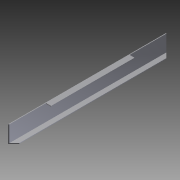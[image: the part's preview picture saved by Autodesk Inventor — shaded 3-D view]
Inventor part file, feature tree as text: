
AUTODESK INVENTOR PART (.ipt)
format: ipt  version: 2012 (Build 160160000, 160)  size: 99,328 bytes
history: native  units: in
note: dims shown in document units (in); Inventor stores cm internally (conversion verified against a paired STEP export)
features: extrude x3, sketch x2
ambient origin geometry x8: Origin, YZ Plane, XZ Plane, XY Plane, X Axis, Y Axis, Z Axis, Center Point
bodies: Solid1 (feature_tree)
feature tree (5):
  extrude  "Extrusion1"  Depth=1.0in
  sketch  "Sketch2"  dims[d2=0.125in d3=0.125in d4=0.125in d5=28.0in d6=0.0in d7=45.0deg d8=0.125in d9=6.5in d10=6.5in d11=28.0in d12=0.0in d13=28.0in d14=0.0in]
  extrude  "Extrusion2"  Depth=0.125in
  extrude  "Extrusion3"  Depth=0.125in
  sketch  "Sketch1"  dims[d0=3.0in d1=1.0in]
